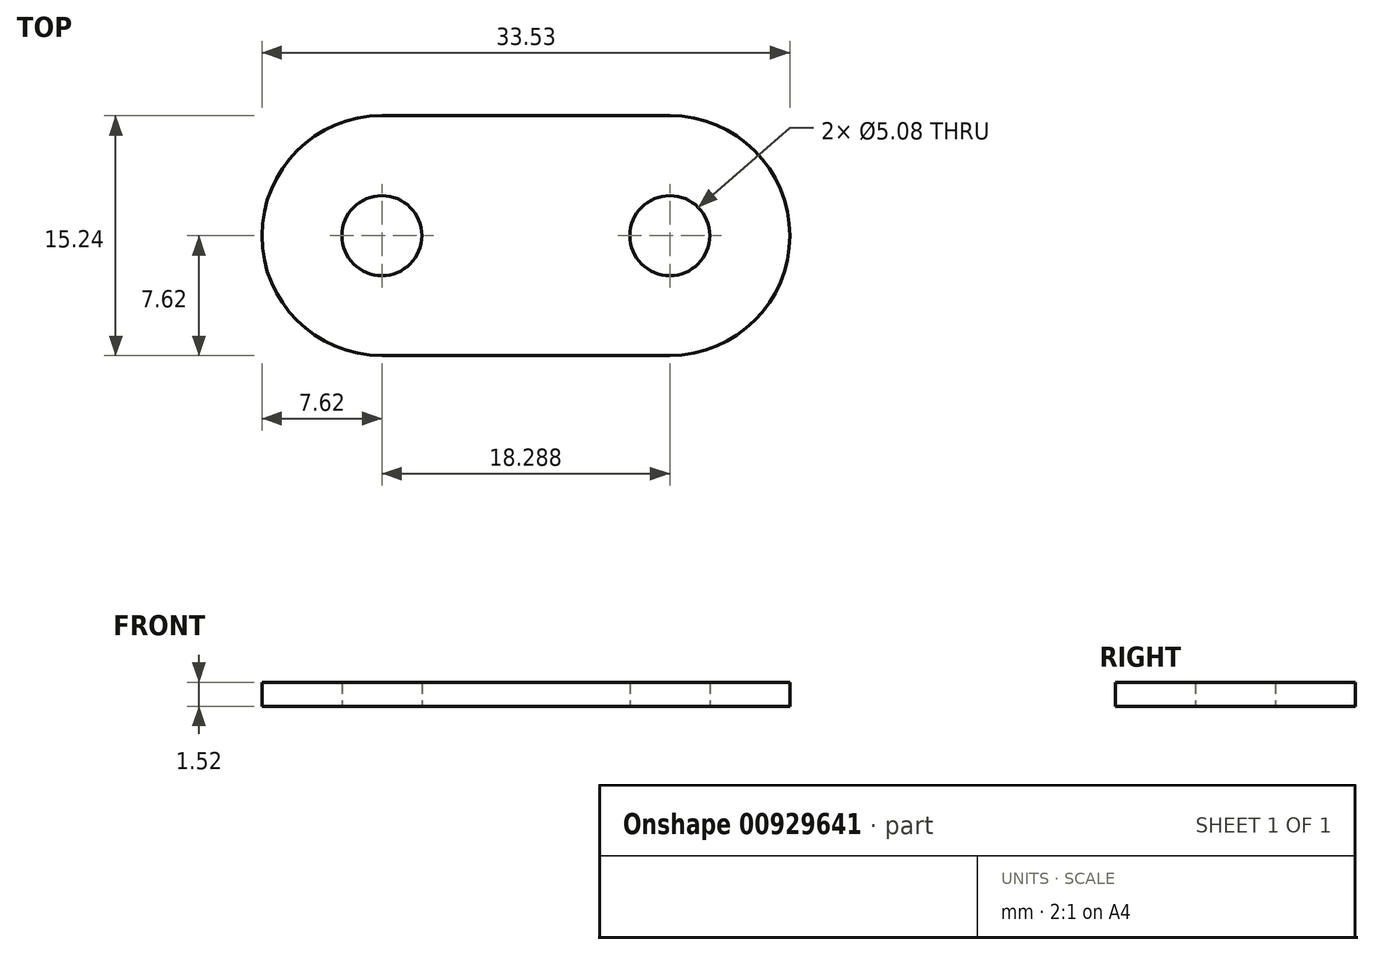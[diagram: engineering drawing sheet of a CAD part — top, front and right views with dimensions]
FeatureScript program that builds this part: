
annotation { "Feature Type Name" : "Feature", "Feature Type Description" : "" }
export const myFeature = defineFeature(function(context is Context, id is Id, definition is map)
    precondition{}
    {
        {
            var Q0;
            Q0=qCreatedBy(makeId("Top.planeOp"),FACE);
            var sketch = newSketch(context, id + "F0", { "sketchPlane" : qUnion([Q0])});
            skCircle(sketch, "E0", {"center": v(0, 0) * mm, "radius": 2.54 * mm});
            skCircle(sketch, "E1", {"center": v(18.29, 0) * mm, "radius": 2.54 * mm});
            skLineSegment(sketch, "E2.bottom", {"start": v(-7.62, 7.62) * mm, "end": v(25.9, 7.62) * mm});
            skLineSegment(sketch, "E2.top", {"start": v(-7.62, -7.62) * mm, "end": v(25.9, -7.62) * mm});
            skLineSegment(sketch, "E2.left", {"start": v(-7.62, 7.62) * mm, "end": v(-7.62, -7.62) * mm});
            skLineSegment(sketch, "E2.right", {"start": v(25.9, 7.62) * mm, "end": v(25.9, -7.62) * mm});
            skArc(sketch, "E3", {"start": v(0, 7.62) * mm, "mid": v(-7.62, 0) * mm, "end": v(0, -7.62) * mm});
            skArc(sketch, "E4", {"start": v(18.29, 7.62) * mm, "mid": v(25.9, 0) * mm, "end": v(18.29, -7.62) * mm});
            skSolve(sketch);
        }
        {
            var Q0;
            Q0=makeQuery(id+"F0.imprint","IMPRINT",FACE,{"disambiguationData":[TD([[makeQuery(id+"F0.imprint","IMPRINT",EDGE,{"derivedFrom":sQuery(id+"F0.wireOp",EDGE,"E0")}),-1.0]])]});
            extrude(context, id + "F1", {"entities" : qUnion([Q0]), "depth" : 1.52 * mm, "offsetDistance" : 25.4 * mm});
        }
    });
